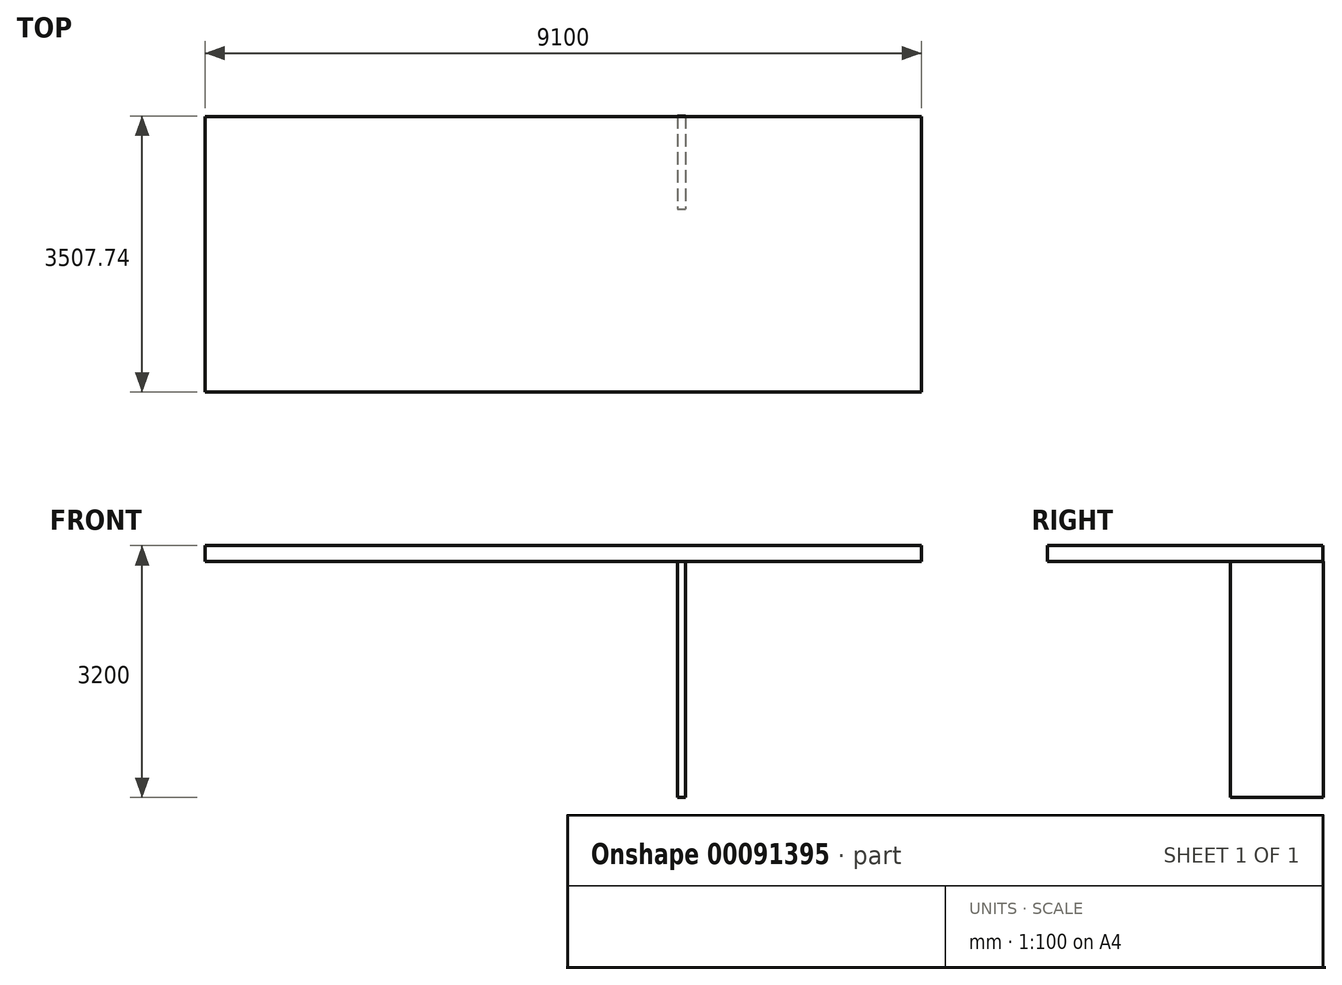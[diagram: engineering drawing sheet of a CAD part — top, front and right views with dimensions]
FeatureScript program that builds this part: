
annotation { "Feature Type Name" : "Feature", "Feature Type Description" : "" }
export const myFeature = defineFeature(function(context is Context, id is Id, definition is map)
    precondition{}
    {
        {
            var Q0;
            Q0=qCreatedBy(makeId("Top.planeOp"),FACE);
            var sketch = newSketch(context, id + "F0", { "sketchPlane" : qUnion([Q0])});
            skLineSegment(sketch, "E0.bottom", {"start": v(-3807.43, 2241.5) * mm, "end": v(5292.57, 2241.5) * mm});
            skLineSegment(sketch, "E0.top", {"start": v(-3807.43, -1258.5) * mm, "end": v(5292.57, -1258.5) * mm});
            skLineSegment(sketch, "E0.left", {"start": v(-3807.43, 2241.5) * mm, "end": v(-3807.43, -1258.5) * mm});
            skLineSegment(sketch, "E0.right", {"start": v(5292.57, 2241.5) * mm, "end": v(5292.57, -1258.5) * mm});
            skSolve(sketch);
        }
        {
            var Q0;
            Q0=qSketchRegion(id+"F0",true);
            extrude(context, id + "F1", {"entities" : qUnion([Q0]), "depth" : 200 * mm});
        }
        {
            var Q0;
            Q0=qCreatedBy(makeId("Top.planeOp"),FACE);
            var sketch = newSketch(context, id + "F2", { "sketchPlane" : qUnion([Q0])});
            skLineSegment(sketch, "E1.bottom", {"start": v(2190.64, 2249.25) * mm, "end": v(2298.12, 2249.25) * mm});
            skLineSegment(sketch, "E1.top", {"start": v(2190.64, 1068.2) * mm, "end": v(2298.12, 1068.2) * mm});
            skLineSegment(sketch, "E1.left", {"start": v(2190.64, 2249.25) * mm, "end": v(2190.64, 1068.2) * mm});
            skLineSegment(sketch, "E1.right", {"start": v(2298.12, 2249.25) * mm, "end": v(2298.12, 1068.2) * mm});
            skSolve(sketch);
        }
        {
            var Q0;
            Q0 = qSketchRegion(id + "F2", true);
            extrude(context, id + "F3", {"entities" : qUnion([Q0]), "oppositeDirection" : true, "depth" : 3000 * mm});
        }
    });
